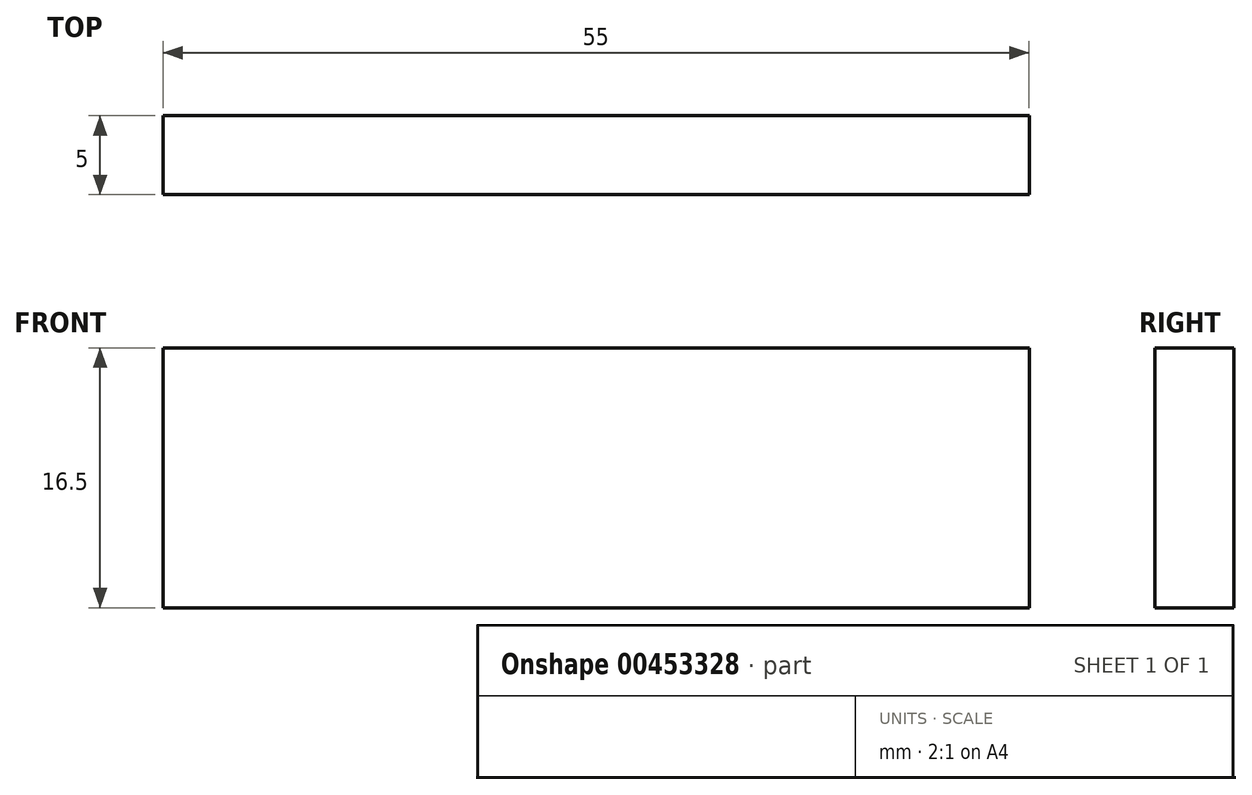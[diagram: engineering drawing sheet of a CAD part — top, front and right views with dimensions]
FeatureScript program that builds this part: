
annotation { "Feature Type Name" : "Feature", "Feature Type Description" : "" }
export const myFeature = defineFeature(function(context is Context, id is Id, definition is map)
    precondition{}
    {
        {
            var Q0;
            Q0=qCreatedBy(makeId("Front.planeOp"),FACE);
            var sketch = newSketch(context, id + "F0", { "sketchPlane" : qUnion([Q0])});
            skLineSegment(sketch, "E0.bottom", {"start": v(-26.55, 4.2) * mm, "end": v(28.45, 4.2) * mm});
            skLineSegment(sketch, "E0.top", {"start": v(-26.55, -12.3) * mm, "end": v(28.45, -12.3) * mm});
            skLineSegment(sketch, "E0.left", {"start": v(-26.55, 4.2) * mm, "end": v(-26.55, -12.3) * mm});
            skLineSegment(sketch, "E0.right", {"start": v(28.45, 4.2) * mm, "end": v(28.45, -12.3) * mm});
            skSolve(sketch);
        }
        {
            var Q0;
            Q0 = qSketchRegion(id + "F0", true);
            extrude(context, id + "F1", {"entities" : qUnion([Q0]), "depth" : 5 * mm});
        }
    });
